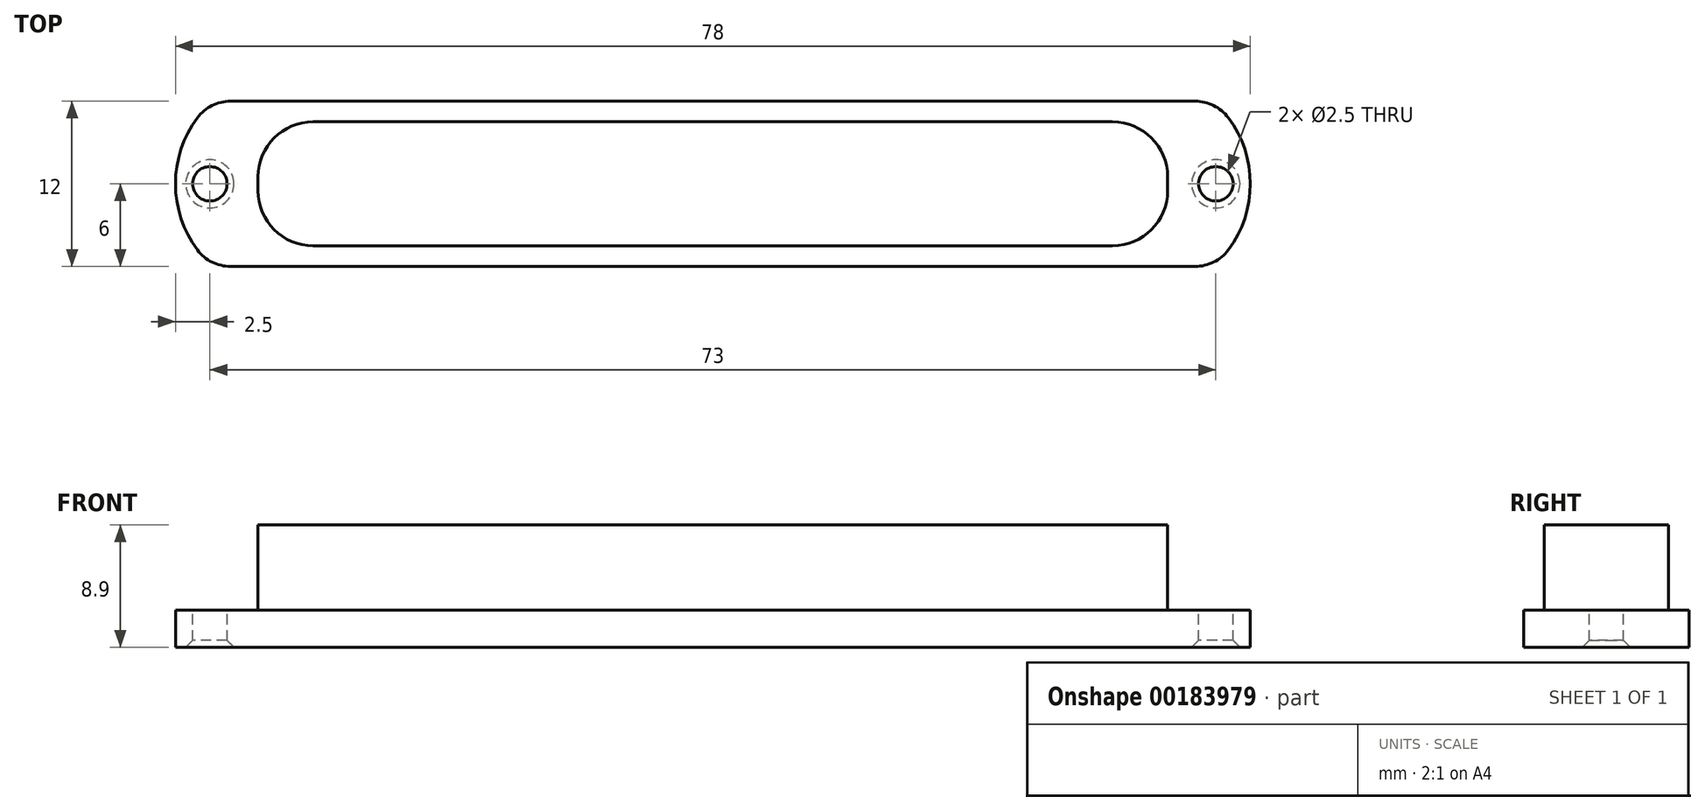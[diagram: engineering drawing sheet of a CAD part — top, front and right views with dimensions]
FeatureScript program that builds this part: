
annotation { "Feature Type Name" : "Feature", "Feature Type Description" : "" }
export const myFeature = defineFeature(function(context is Context, id is Id, definition is map)
    precondition{}
    {
        {
            var Q0;
            Q0=qCreatedBy(makeId("Top.planeOp"),FACE);
            var sketch = newSketch(context, id + "F0", { "sketchPlane" : qUnion([Q0])});
            skLineSegment(sketch, "E0.bottom", {"start": v(35, -6) * mm, "end": v(-35, -6) * mm});
            skLineSegment(sketch, "E0.top", {"start": v(35, 6) * mm, "end": v(-35, 6) * mm});
            skPoint(sketch, "E0.middle", {"position": v(0, 0) * mm});
            skLineSegment(sketch, "E1", {"start": v(39, 0) * mm, "end": v(31, 0) * mm, "construction": true});
            skPoint(sketch, "E1.endSnap0", {"position": v(39, 0) * mm});
            skArc(sketch, "E2", {"start": v(37.4, -4.8) * mm, "mid": v(39, 0) * mm, "end": v(37.4, 4.8) * mm});
            skPoint(sketch, "E3.orphan", {"position": v(39, 6) * mm});
            skArc(sketch, "E4.MirrorCS", {"start": v(-37.4, -4.8) * mm, "mid": v(-39, 0) * mm, "end": v(-37.4, 4.8) * mm});
            skLineSegment(sketch, "E5", {"start": v(-39, 0) * mm, "end": v(39, 0) * mm, "construction": true});
            skPoint(sketch, "E6.orphan", {"position": v(-39, -6) * mm});
            skPoint(sketch, "E7.visualSharp", {"position": v(-36.3, -6) * mm});
            skArc(sketch, "E7.filletArc", {"start": v(-37.4, -4.8) * mm, "mid": v(-36.34, -5.68) * mm, "end": v(-35, -6) * mm});
            skPoint(sketch, "E8.visualSharp", {"position": v(-36.3, 6) * mm});
            skArc(sketch, "E8.filletArc", {"start": v(-35, 6) * mm, "mid": v(-36.34, 5.68) * mm, "end": v(-37.4, 4.8) * mm});
            skPoint(sketch, "E9.visualSharp", {"position": v(36.3, -6) * mm});
            skArc(sketch, "E9.filletArc", {"start": v(35, -6) * mm, "mid": v(36.34, -5.68) * mm, "end": v(37.4, -4.8) * mm});
            skPoint(sketch, "E10.visualSharp", {"position": v(36.3, 6) * mm});
            skArc(sketch, "E10.filletArc", {"start": v(37.4, 4.8) * mm, "mid": v(36.34, 5.68) * mm, "end": v(35, 6) * mm});
            skSolve(sketch);
        }
        {
            var Q0;
            Q0 = qSketchRegion(id + "F0", true);
            extrude(context, id + "F1", {"entities" : qUnion([Q0]), "depth" : 2.7 * mm});
        }
        {
            var Q0;
            Q0=makeQuery(id+"F1.opExtrude","CAP_FACE",FACE,{"disambiguationData":[OSD([sQuery(id+"F0.wireOp",EDGE,"E0.bottom"),sQuery(id+"F0.wireOp",EDGE,"E0.top"),sQuery(id+"F0.wireOp",EDGE,"E2"),sQuery(id+"F0.wireOp",EDGE,"E4.MirrorCS"),sQuery(id+"F0.wireOp",EDGE,"E7.filletArc"),sQuery(id+"F0.wireOp",EDGE,"E8.filletArc"),sQuery(id+"F0.wireOp",EDGE,"E9.filletArc"),sQuery(id+"F0.wireOp",EDGE,"E10.filletArc")])],"isStart":false});
            var sketch = newSketch(context, id + "F2", { "sketchPlane" : qUnion([Q0])});
            skLineSegment(sketch, "E11.bottom", {"start": v(-29, 4.5) * mm, "end": v(29, 4.5) * mm});
            skLineSegment(sketch, "E11.top", {"start": v(-29, -4.5) * mm, "end": v(29, -4.5) * mm});
            skLineSegment(sketch, "E11.left", {"start": v(-33, 0.5) * mm, "end": v(-33, -0.5) * mm});
            skLineSegment(sketch, "E11.right", {"start": v(33, 0.5) * mm, "end": v(33, -0.5) * mm});
            skPoint(sketch, "E11.middle", {"position": v(0, 0) * mm});
            skPoint(sketch, "E12.visualSharp", {"position": v(-33, 4.5) * mm});
            skArc(sketch, "E12.filletArc", {"start": v(-29, 4.5) * mm, "mid": v(-31.83, 3.33) * mm, "end": v(-33, 0.5) * mm});
            skPoint(sketch, "E13.visualSharp", {"position": v(-33, -4.5) * mm});
            skArc(sketch, "E13.filletArc", {"start": v(-33, -0.5) * mm, "mid": v(-31.83, -3.33) * mm, "end": v(-29, -4.5) * mm});
            skPoint(sketch, "E14.visualSharp", {"position": v(33, -4.5) * mm});
            skArc(sketch, "E14.filletArc", {"start": v(29, -4.5) * mm, "mid": v(31.83, -3.33) * mm, "end": v(33, -0.5) * mm});
            skPoint(sketch, "E15.visualSharp", {"position": v(33, 4.5) * mm});
            skArc(sketch, "E15.filletArc", {"start": v(33, 0.5) * mm, "mid": v(31.83, 3.33) * mm, "end": v(29, 4.5) * mm});
            skSolve(sketch);
        }
        {
            var Q0;
            Q0 = qSketchRegion(id + "F2", true);
            extrude(context, id + "F3", {"entities" : qUnion([Q0]), "operationType" : NewBodyOperationType.ADD, "depth" : 6.2 * mm});
        }
        {
            var Q0;
            Q0=makeQuery(id+"F1.opExtrude","CAP_FACE",FACE,{"disambiguationData":[OSD([sQuery(id+"F0.wireOp",EDGE,"E0.bottom"),sQuery(id+"F0.wireOp",EDGE,"E0.top"),sQuery(id+"F0.wireOp",EDGE,"E2"),sQuery(id+"F0.wireOp",EDGE,"E4.MirrorCS"),sQuery(id+"F0.wireOp",EDGE,"E7.filletArc"),sQuery(id+"F0.wireOp",EDGE,"E8.filletArc"),sQuery(id+"F0.wireOp",EDGE,"E9.filletArc"),sQuery(id+"F0.wireOp",EDGE,"E10.filletArc")])],"isStart":false});
            var sketch = newSketch(context, id + "F4", { "sketchPlane" : qUnion([Q0])});
            skLineSegment(sketch, "E16", {"start": v(-39, 0) * mm, "end": v(-36.5, 0) * mm, "construction": true});
            skPoint(sketch, "E16.endSnap0", {"position": v(-39, 0) * mm});
            skCircle(sketch, "E17", {"center": v(-36.5, 0) * mm, "radius": 1.25 * mm});
            skLineSegment(sketch, "E18", {"start": v(0, -6) * mm, "end": v(0, 0) * mm, "construction": true});
            skCircle(sketch, "E19.MirrorC", {"center": v(36.5, 0) * mm, "radius": 1.25 * mm});
            skSolve(sketch);
        }
        {
            var Q0;
            Q0 = qSketchRegion(id + "F4", true);
            extrude(context, id + "F5", {"entities" : qUnion([Q0]), "operationType" : NewBodyOperationType.REMOVE, "oppositeDirection" : true, "depth" : 25 * mm});
        }
        {
            var Q0;
            Q0=makeQuery(id+"F5.boolean.opBoolean","INTERSECT",EDGE,{"derivedFrom":[makeQuery(id+"F1.opExtrude","CAP_FACE",FACE,{"disambiguationData":[OSD([sQuery(id+"F0.wireOp",EDGE,"E0.bottom"),sQuery(id+"F0.wireOp",EDGE,"E0.top"),sQuery(id+"F0.wireOp",EDGE,"E2"),sQuery(id+"F0.wireOp",EDGE,"E4.MirrorCS"),sQuery(id+"F0.wireOp",EDGE,"E7.filletArc"),sQuery(id+"F0.wireOp",EDGE,"E8.filletArc"),sQuery(id+"F0.wireOp",EDGE,"E9.filletArc"),sQuery(id+"F0.wireOp",EDGE,"E10.filletArc")])],"isStart":true}),makeQuery(id+"F5.opExtrude","SWEPT_FACE",FACE,{"disambiguationData":[OSD([sQuery(id+"F4.wireOp",EDGE,"E17")])]})]});
            var Q1;
            Q1=makeQuery(id+"F5.boolean.opBoolean","INTERSECT",EDGE,{"derivedFrom":[makeQuery(id+"F1.opExtrude","CAP_FACE",FACE,{"disambiguationData":[OSD([sQuery(id+"F0.wireOp",EDGE,"E0.bottom"),sQuery(id+"F0.wireOp",EDGE,"E0.top"),sQuery(id+"F0.wireOp",EDGE,"E2"),sQuery(id+"F0.wireOp",EDGE,"E4.MirrorCS"),sQuery(id+"F0.wireOp",EDGE,"E7.filletArc"),sQuery(id+"F0.wireOp",EDGE,"E8.filletArc"),sQuery(id+"F0.wireOp",EDGE,"E9.filletArc"),sQuery(id+"F0.wireOp",EDGE,"E10.filletArc")])],"isStart":true}),makeQuery(id+"F5.opExtrude","SWEPT_FACE",FACE,{"disambiguationData":[OSD([sQuery(id+"F4.wireOp",EDGE,"E19.MirrorC")])]})]});
            chamfer(context, id + "F6", {"entities" : qUnion([Q0, Q1]), "width" : 0.5 * mm, "tangentPropagation" : true});
        }
    });
